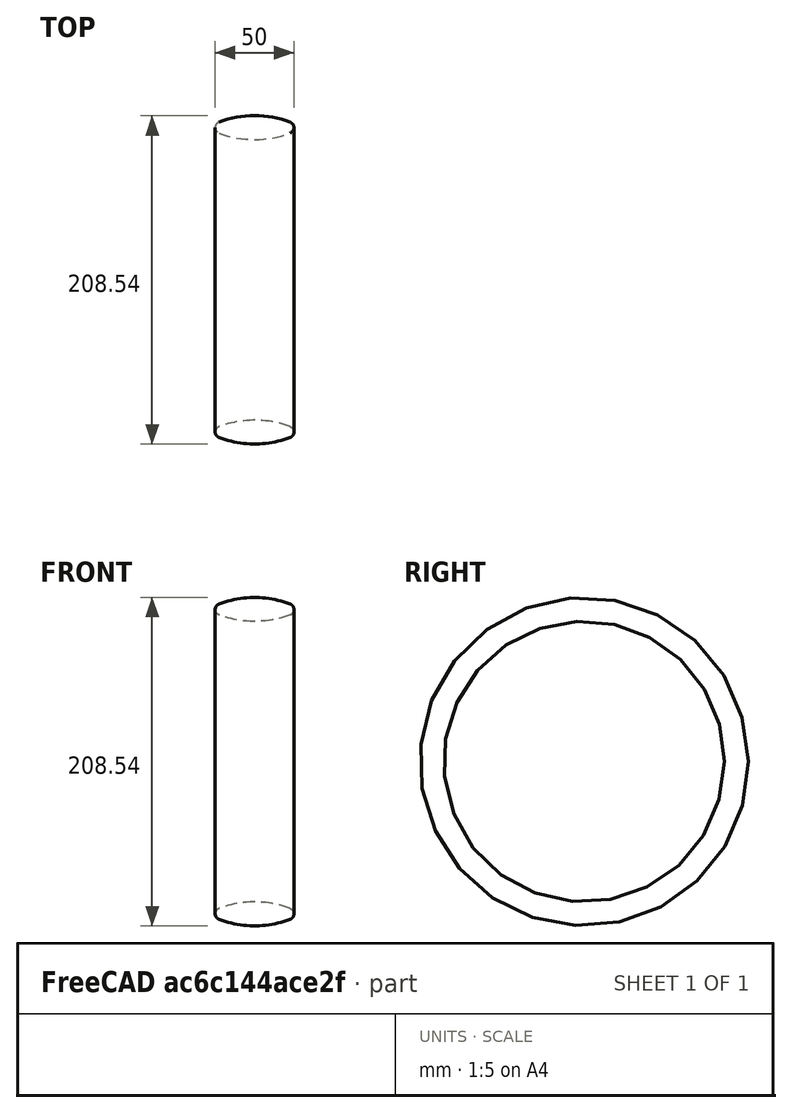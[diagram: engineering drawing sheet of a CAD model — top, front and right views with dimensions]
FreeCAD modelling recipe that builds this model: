
FCSTD DOCUMENT
Label: gyuru_volume_test_p3
objects: Sketcher::SketchObject×1, Part::Revolution×1
note: 2 computed .brp shape members not serialized (recipe doc carries the construction recipe); baked Part::Feature solids carry a one-line shape summary decoded from their .brp

FEATURE [Sketcher::SketchObject] Sketch
  sketch-geometry (8):
    g0: LineSegment [constr] StartX=50 StartY=153.007 StartZ=0 EndX=50 EndY=25.1744 EndZ=0
    g1: LineSegment [constr] StartX=-10.5525 StartY=89.127 StartZ=0 EndX=91.3895 EndY=89.127 EndZ=0
    g2: LineSegment [constr] StartX=-21.5219 StartY=104.27 StartZ=0 EndX=96.4869 EndY=104.27 EndZ=0
    g3: ArcOfCircle CenterX=25 CenterY=40.47 CenterZ=0 NormalX=0 NormalY=0 NormalZ=1 Radius=63.8 StartAngle=1.20802 EndAngle=1.93357
    g4: ArcOfCircle CenterX=25 CenterY=152.927 CenterZ=0 NormalX=0 NormalY=0 NormalZ=1 Radius=63.8 StartAngle=4.34961 EndAngle=5.07516
    g5: ArcOfCircle CenterX=3.65716 CenterY=96.6985 CenterZ=0 NormalX=0 NormalY=0 NormalZ=1 Radius=3.65716 StartAngle=1.93357 EndAngle=4.34961
    g6: ArcOfCircle CenterX=46.3428 CenterY=96.6985 CenterZ=0 NormalX=0 NormalY=0 NormalZ=1 Radius=3.65716 StartAngle=5.07516 EndAngle=7.49121
    g7: LineSegment [constr] StartX=0 StartY=133.551 StartZ=0 EndX=0 EndY=65.1141 EndZ=0
  constraints (20):
    c: Vertical(g0)
    c: DistanceX(g0) = 50
    c: Horizontal(g1)
    c: DistanceY(g1) = 89.127
    c: Horizontal(g2)
    c: DistanceY(g2) = 104.27
    c: Radius(g3) = 63.8
    c: Radius(g4) = 63.8
    c: Tangent(g3,g2)
    c: Tangent(g4,g1)
    c: DistanceX(g3) = 25
    c: DistanceX(g4) = 25
    c: Tangent(g5,g4)
    c: Tangent(g5,g3)
    c: Tangent(g4,g6)
    c: Tangent(g3,g6)
    c: Tangent(g6,g0)
    c: PointOnObject(g7,g-2)
    c: PointOnObject(g7,g-2)
    c: Tangent(g7,g5)
FEATURE [Part::Revolution] Revolve
  Angle = 360
  Axis = (1,0,0)
  Base = (0,0,0)
  Source = -> Sketch
